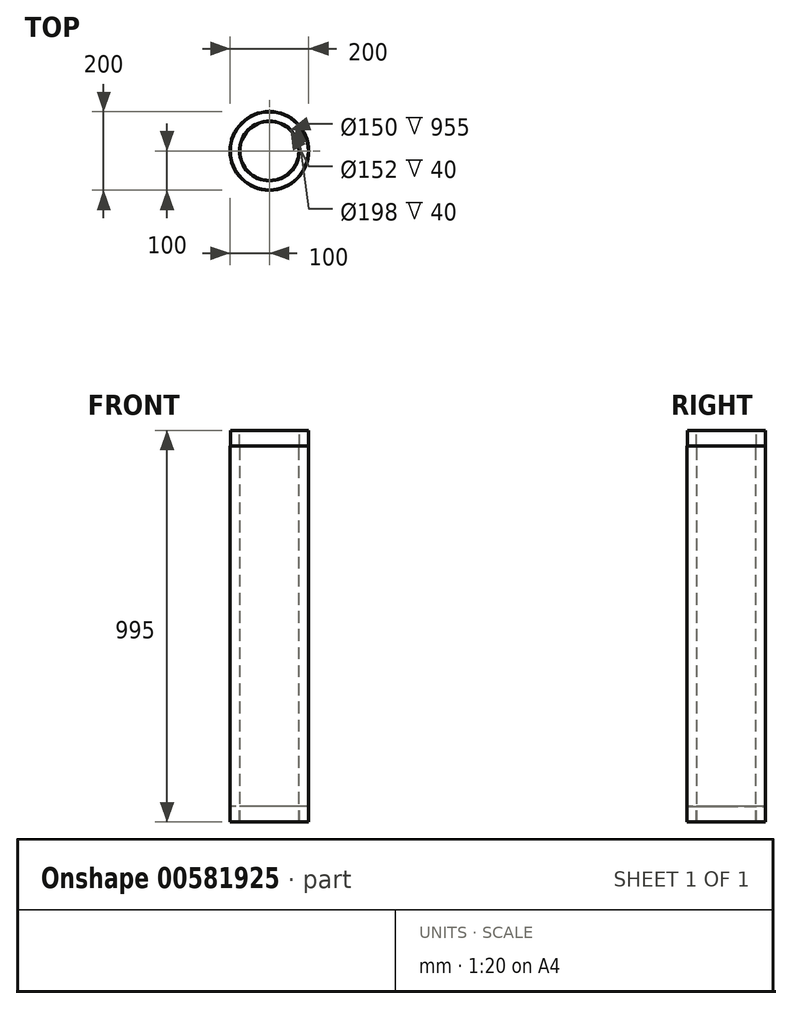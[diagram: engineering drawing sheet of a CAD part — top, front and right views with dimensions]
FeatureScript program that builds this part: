
annotation { "Feature Type Name" : "Feature", "Feature Type Description" : "" }
export const myFeature = defineFeature(function(context is Context, id is Id, definition is map)
    precondition{}
    {
        {
            var Q0;
            Q0=qCreatedBy(makeId("Front.planeOp"),FACE);
            var sketch = newSketch(context, id + "F0", { "sketchPlane" : qUnion([Q0])});
            skLineSegment(sketch, "E0", {"start": v(0, 345.75) * mm, "end": v(0, -558.03) * mm, "construction": true});
            skLineSegment(sketch, "E1", {"start": v(-75, -518.84) * mm, "end": v(-75, 436.16) * mm});
            skLineSegment(sketch, "E2", {"start": v(-75, 436.16) * mm, "end": v(-76, 436.16) * mm});
            skLineSegment(sketch, "E3", {"start": v(-76, 436.16) * mm, "end": v(-76, 476.16) * mm});
            skLineSegment(sketch, "E4", {"start": v(-76, 476.16) * mm, "end": v(-99, 476.16) * mm});
            skLineSegment(sketch, "E5", {"start": v(-99, 476.16) * mm, "end": v(-99, 436.16) * mm});
            skLineSegment(sketch, "E6", {"start": v(-99, 436.16) * mm, "end": v(-100, 436.16) * mm});
            skLineSegment(sketch, "E7", {"start": v(-100, 436.16) * mm, "end": v(-100, -518.84) * mm});
            skLineSegment(sketch, "E8", {"start": v(-100, -518.84) * mm, "end": v(-99, -518.84) * mm});
            skLineSegment(sketch, "E9", {"start": v(-99, -518.84) * mm, "end": v(-99, -478.84) * mm});
            skLineSegment(sketch, "E10", {"start": v(-99, -478.84) * mm, "end": v(-76, -478.84) * mm});
            skLineSegment(sketch, "E11", {"start": v(-76, -478.84) * mm, "end": v(-76, -518.84) * mm});
            skLineSegment(sketch, "E12", {"start": v(-76, -518.84) * mm, "end": v(-75, -518.84) * mm});
            skSolve(sketch);
        }
        {
            var Q0;
            Q0=qSketchRegion(id+"F0",true);
            var Q1;
            Q1=sQuery(id+"F0.wireOp",EDGE,"E0");
            revolve(context, id + "F1", {"entities" : qUnion([Q0]), "axis" : qUnion([Q1]), "revolveType" : RevolveType.FULL});
        }
    });
